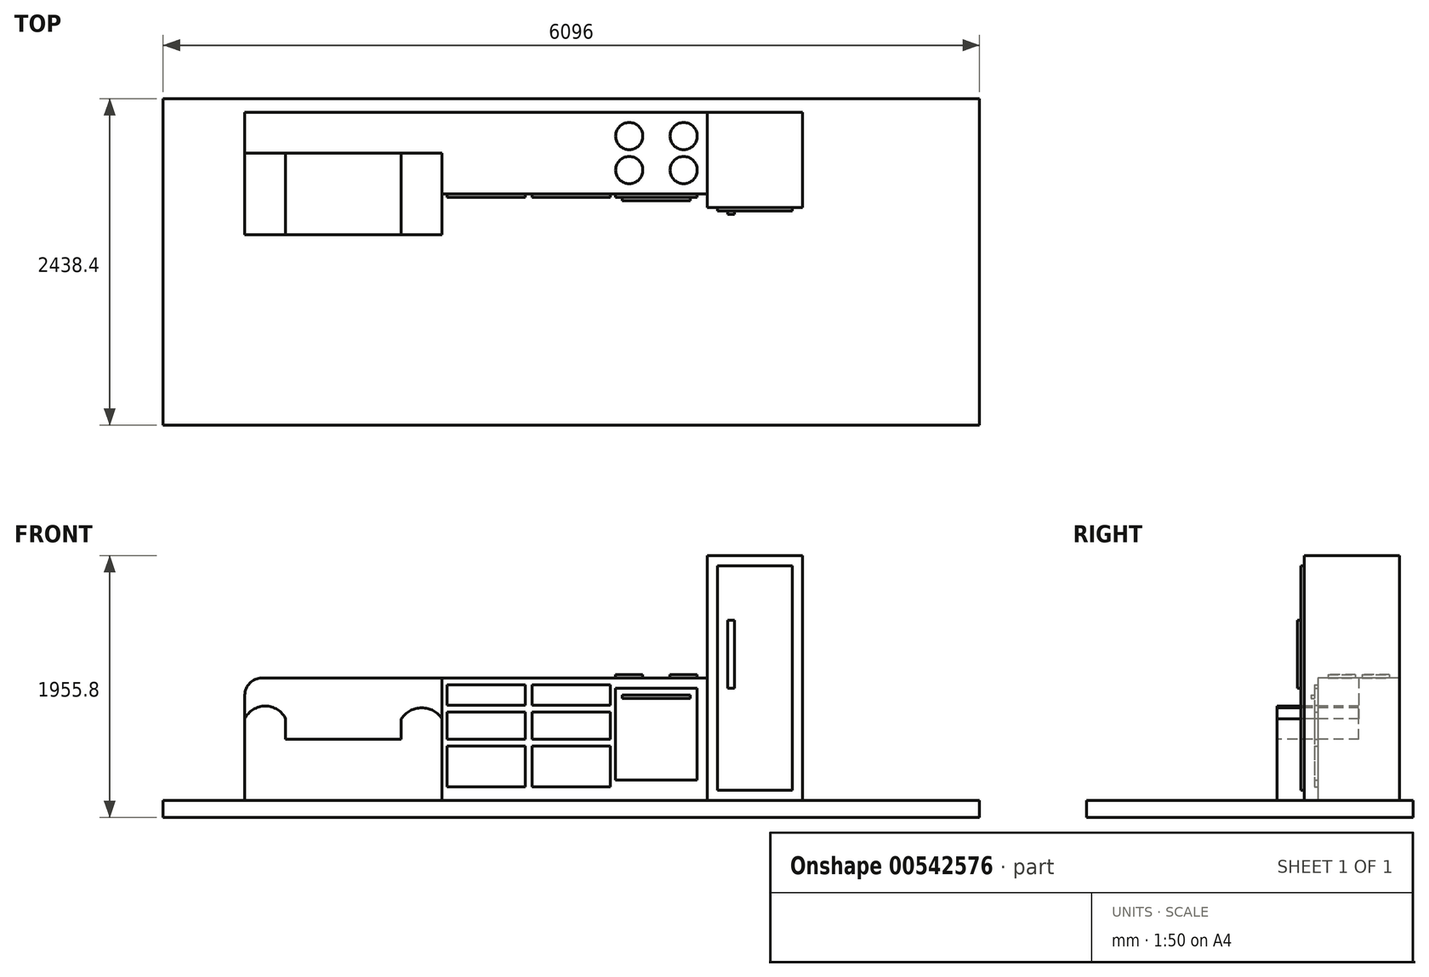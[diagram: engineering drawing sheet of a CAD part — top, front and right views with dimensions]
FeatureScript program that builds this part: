
annotation { "Feature Type Name" : "Feature", "Feature Type Description" : "" }
export const myFeature = defineFeature(function(context is Context, id is Id, definition is map)
    precondition{}
    {
        {
            var Q0;
            Q0=qCreatedBy(makeId("Top.planeOp"),FACE);
            var sketch = newSketch(context, id + "F0", { "sketchPlane" : qUnion([Q0])});
            skLineSegment(sketch, "E0.bottom", {"start": v(-1992.71, 1218.7) * mm, "end": v(4103.29, 1218.7) * mm});
            skLineSegment(sketch, "E0.top", {"start": v(-1992.71, -1219.7) * mm, "end": v(4103.29, -1219.7) * mm});
            skLineSegment(sketch, "E0.left", {"start": v(-1992.71, 1218.7) * mm, "end": v(-1992.71, -1219.7) * mm});
            skLineSegment(sketch, "E0.right", {"start": v(4103.29, 1218.7) * mm, "end": v(4103.29, -1219.7) * mm});
            skSolve(sketch);
        }
        {
            var Q0;
            Q0=makeQuery(id+"F0.imprint","IMPRINT",FACE,{"disambiguationData":[TD([[makeQuery(id+"F0.imprint","IMPRINT",EDGE,{"derivedFrom":sQuery(id+"F0.wireOp",EDGE,"E0.bottom")}),-1.0]])]});
            extrude(context, id + "F1", {"entities" : qUnion([Q0]), "depth" : 127 * mm, "offsetDistance" : 25.4 * mm});
        }
        {
            var Q0;
            Q0=makeQuery(id+"F1.opExtrude","CAP_FACE",FACE,{"disambiguationData":[OSD([sQuery(id+"F0.wireOp",EDGE,"E0.bottom"),sQuery(id+"F0.wireOp",EDGE,"E0.top"),sQuery(id+"F0.wireOp",EDGE,"E0.left"),sQuery(id+"F0.wireOp",EDGE,"E0.right")])],"isStart":false});
            var sketch = newSketch(context, id + "F2", { "sketchPlane" : qUnion([Q0])});
            skLineSegment(sketch, "E1.bottom", {"start": v(-1383.11, 1117.1) * mm, "end": v(2071.29, 1117.1) * mm});
            skLineSegment(sketch, "E1.top", {"start": v(90.09, 507.5) * mm, "end": v(2071.29, 507.5) * mm});
            skLineSegment(sketch, "E1.left", {"start": v(-1383.11, 1117.1) * mm, "end": v(-1383.11, 507.5) * mm});
            skLineSegment(sketch, "E1.right", {"start": v(2071.29, 1117.1) * mm, "end": v(2071.29, 507.5) * mm});
            skLineSegment(sketch, "E2.bottom", {"start": v(2782.49, 1117.1) * mm, "end": v(2071.29, 1117.1) * mm});
            skLineSegment(sketch, "E2.top", {"start": v(2782.49, 405.9) * mm, "end": v(2071.29, 405.9) * mm});
            skLineSegment(sketch, "E2.left", {"start": v(2782.49, 1117.1) * mm, "end": v(2782.49, 405.9) * mm});
            skLineSegment(sketch, "E2.right", {"start": v(2071.29, 1117.1) * mm, "end": v(2071.29, 405.9) * mm});
            skLineSegment(sketch, "E3.top", {"start": v(-1383.11, 202.7) * mm, "end": v(90.09, 202.7) * mm});
            skLineSegment(sketch, "E3.left", {"start": v(-1383.11, 507.5) * mm, "end": v(-1383.11, 202.7) * mm});
            skLineSegment(sketch, "E3.right", {"start": v(90.09, 507.5) * mm, "end": v(90.09, 202.7) * mm});
            skLineSegment(sketch, "E4", {"start": v(90.09, 507.5) * mm, "end": v(90.09, 1117.1) * mm});
            skLineSegment(sketch, "E5", {"start": v(1309.29, 507.5) * mm, "end": v(1309.29, 1117.1) * mm});
            skSolve(sketch);
        }
        {
            var Q0;
            {var subQ0=sQuery(id+"F2.wireOp",EDGE,"E1.left");Q0=makeQuery(id+"F2.imprint","IMPRINT",FACE,{"disambiguationData":[TD([[makeQuery(id+"F2.imprint","IMPRINT",EDGE,{"derivedFrom":subQ0}),1.0]])]});}
            var Q1;
            {var subQ0=sQuery(id+"F2.wireOp",EDGE,"E4");Q1=makeQuery(id+"F2.imprint","IMPRINT",FACE,{"disambiguationData":[TD([[makeQuery(id+"F2.imprint","IMPRINT",EDGE,{"derivedFrom":subQ0}),-1.0]])]});}
            var Q2;
            {var subQ3=sQuery(id+"F2.wireOp",EDGE,"E5");Q2=makeQuery(id+"F2.imprint","IMPRINT",FACE,{"disambiguationData":[TD([[makeQuery(id+"F2.imprint","IMPRINT",EDGE,{"derivedFrom":subQ3}),-1.0]])]});}
            extrude(context, id + "F3", {"entities" : qUnion([Q0, Q1, Q2]), "operationType" : NewBodyOperationType.ADD, "depth" : 914.4 * mm, "offsetDistance" : 25.4 * mm});
        }
        {
            var Q0;
            {var subQ1=sQuery(id+"F2.wireOp",EDGE,"E2.bottom");Q0=makeQuery(id+"F2.imprint","IMPRINT",FACE,{"disambiguationData":[TD([[makeQuery(id+"F2.imprint","IMPRINT",EDGE,{"derivedFrom":subQ1}),1.0]])]});}
            extrude(context, id + "F4", {"entities" : qUnion([Q0]), "operationType" : NewBodyOperationType.ADD, "depth" : 1828.8 * mm, "offsetDistance" : 25.4 * mm});
        }
        {
            var Q0;
            Q0=makeQuery(id+"F3.opExtrude","CAP_FACE",FACE,{"disambiguationData":[OSD([sQuery(id+"F2.wireOp",EDGE,"E1.bottom"),sQuery(id+"F2.wireOp",EDGE,"E1.top"),sQuery(id+"F2.wireOp",EDGE,"E1.left"),sQuery(id+"F2.wireOp",EDGE,"E2.right"),sQuery(id+"F2.wireOp",EDGE,"E3.top"),sQuery(id+"F2.wireOp",EDGE,"E3.left"),sQuery(id+"F2.wireOp",EDGE,"E3.right")])],"isStart":false});
            var sketch = newSketch(context, id + "F5", { "sketchPlane" : qUnion([Q0])});
            skLineSegment(sketch, "E6", {"start": v(1309.29, 1117.1) * mm, "end": v(1309.29, 507.5) * mm});
            skLineSegment(sketch, "E7.bottom", {"start": v(1487.09, 939.3) * mm, "end": v(1893.49, 939.3) * mm, "construction": true});
            skLineSegment(sketch, "E7.top", {"start": v(1487.09, 685.3) * mm, "end": v(1893.49, 685.3) * mm, "construction": true});
            skLineSegment(sketch, "E7.left", {"start": v(1487.09, 939.3) * mm, "end": v(1487.09, 685.3) * mm, "construction": true});
            skLineSegment(sketch, "E7.right", {"start": v(1893.49, 939.3) * mm, "end": v(1893.49, 685.3) * mm, "construction": true});
            skPoint(sketch, "E7.middle", {"position": v(1690.29, 812.3) * mm});
            skCircle(sketch, "E8", {"center": v(1487.09, 939.3) * mm, "radius": 101.6 * mm});
            skCircle(sketch, "E9", {"center": v(1893.49, 939.3) * mm, "radius": 101.6 * mm});
            skCircle(sketch, "E10", {"center": v(1893.49, 685.3) * mm, "radius": 101.6 * mm});
            skCircle(sketch, "E11", {"center": v(1487.09, 685.3) * mm, "radius": 101.6 * mm});
            skSolve(sketch);
        }
        {
            var Q0;
            Q0=makeQuery(id+"F5.imprint","IMPRINT",FACE,{"disambiguationData":[TD([[makeQuery(id+"F5.imprint","IMPRINT",EDGE,{"derivedFrom":sQuery(id+"F5.wireOp",EDGE,"E9")}),1.0]])]});
            var Q1;
            Q1=makeQuery(id+"F5.imprint","IMPRINT",FACE,{"disambiguationData":[TD([[makeQuery(id+"F5.imprint","IMPRINT",EDGE,{"derivedFrom":sQuery(id+"F5.wireOp",EDGE,"E8")}),1.0]])]});
            var Q2;
            Q2=makeQuery(id+"F5.imprint","IMPRINT",FACE,{"disambiguationData":[TD([[makeQuery(id+"F5.imprint","IMPRINT",EDGE,{"derivedFrom":sQuery(id+"F5.wireOp",EDGE,"E11")}),1.0]])]});
            var Q3;
            Q3=makeQuery(id+"F5.imprint","IMPRINT",FACE,{"disambiguationData":[TD([[makeQuery(id+"F5.imprint","IMPRINT",EDGE,{"derivedFrom":sQuery(id+"F5.wireOp",EDGE,"E10")}),1.0]])]});
            extrude(context, id + "F6", {"entities" : qUnion([Q0, Q1, Q2, Q3]), "operationType" : NewBodyOperationType.ADD, "depth" : 25.4 * mm, "offsetDistance" : 25.4 * mm});
        }
        {
            var Q0;
            Q0=makeQuery(id+"F3.opExtrude","SWEPT_FACE",FACE,{"disambiguationData":[OSD([sQuery(id+"F2.wireOp",EDGE,"E1.top")])]});
            var sketch = newSketch(context, id + "F7", { "sketchPlane" : qUnion([Q0])});
            skLineSegment(sketch, "E12", {"start": v(1309.29, 1041.4) * mm, "end": v(1309.29, 127) * mm});
            skLineSegment(sketch, "E13.bottom", {"start": v(1385.49, 965.2) * mm, "end": v(1995.09, 965.2) * mm});
            skLineSegment(sketch, "E13.top", {"start": v(1385.49, 279.4) * mm, "end": v(1995.09, 279.4) * mm});
            skLineSegment(sketch, "E13.left", {"start": v(1385.49, 965.2) * mm, "end": v(1385.49, 279.4) * mm});
            skLineSegment(sketch, "E13.right", {"start": v(1995.09, 965.2) * mm, "end": v(1995.09, 279.4) * mm});
            skPoint(sketch, "E13.middle", {"position": v(1690.29, 622.3) * mm});
            skSolve(sketch);
        }
        {
            var Q0;
            Q0=makeQuery(id+"F7.imprint","IMPRINT",FACE,{"disambiguationData":[TD([[makeQuery(id+"F7.imprint","IMPRINT",EDGE,{"derivedFrom":sQuery(id+"F7.wireOp",EDGE,"E13.bottom")}),-1.0]])]});
            extrude(context, id + "F8", {"entities" : qUnion([Q0]), "operationType" : NewBodyOperationType.ADD, "depth" : 25.4 * mm, "offsetDistance" : 25.4 * mm});
        }
        {
            var Q0;
            Q0=makeQuery(id+"F8.opExtrude","CAP_FACE",FACE,{"disambiguationData":[OSD([sQuery(id+"F7.wireOp",EDGE,"E13.bottom"),sQuery(id+"F7.wireOp",EDGE,"E13.top"),sQuery(id+"F7.wireOp",EDGE,"E13.left"),sQuery(id+"F7.wireOp",EDGE,"E13.right")])],"isStart":false});
            var sketch = newSketch(context, id + "F9", { "sketchPlane" : qUnion([Q0])});
            skLineSegment(sketch, "E14.bottom", {"start": v(1436.29, 914.4) * mm, "end": v(1944.29, 914.4) * mm});
            skLineSegment(sketch, "E14.top", {"start": v(1436.29, 889) * mm, "end": v(1944.29, 889) * mm});
            skLineSegment(sketch, "E14.left", {"start": v(1436.29, 914.4) * mm, "end": v(1436.29, 889) * mm});
            skLineSegment(sketch, "E14.right", {"start": v(1944.29, 914.4) * mm, "end": v(1944.29, 889) * mm});
            skPoint(sketch, "E14.middle", {"position": v(1690.29, 901.7) * mm});
            skSolve(sketch);
        }
        {
            var Q0;
            Q0=makeQuery(id+"F9.imprint","IMPRINT",FACE,{"disambiguationData":[TD([[makeQuery(id+"F9.imprint","IMPRINT",EDGE,{"derivedFrom":sQuery(id+"F9.wireOp",EDGE,"E14.bottom")}),-1.0]])]});
            extrude(context, id + "F10", {"entities" : qUnion([Q0]), "operationType" : NewBodyOperationType.ADD, "depth" : 25.4 * mm, "offsetDistance" : 25.4 * mm});
        }
        {
            var Q0;
            Q0=makeQuery(id+"F4.opExtrude","SWEPT_FACE",FACE,{"disambiguationData":[OSD([sQuery(id+"F2.wireOp",EDGE,"E2.top")])]});
            var sketch = newSketch(context, id + "F11", { "sketchPlane" : qUnion([Q0])});
            skLineSegment(sketch, "E15.0", {"start": v(2147.49, 203.2) * mm, "end": v(2706.29, 203.2) * mm});
            skLineSegment(sketch, "E15.1", {"start": v(2147.49, 1879.6) * mm, "end": v(2147.49, 203.2) * mm});
            skLineSegment(sketch, "E15.2", {"start": v(2706.29, 1879.6) * mm, "end": v(2147.49, 1879.6) * mm});
            skLineSegment(sketch, "E15.3", {"start": v(2706.29, 203.2) * mm, "end": v(2706.29, 1879.6) * mm});
            skSolve(sketch);
        }
        {
            var Q0;
            Q0=makeQuery(id+"F11.imprint","IMPRINT",FACE,{"disambiguationData":[TD([[makeQuery(id+"F11.imprint","IMPRINT",EDGE,{"derivedFrom":sQuery(id+"F11.wireOp",EDGE,"E15.0")}),1.0]])]});
            extrude(context, id + "F12", {"entities" : qUnion([Q0]), "operationType" : NewBodyOperationType.ADD, "depth" : 25.4 * mm, "offsetDistance" : 25.4 * mm});
        }
        {
            var Q0;
            Q0=makeQuery(id+"F12.opExtrude","CAP_FACE",FACE,{"disambiguationData":[OSD([sQuery(id+"F11.wireOp",EDGE,"E15.0"),sQuery(id+"F11.wireOp",EDGE,"E15.1"),sQuery(id+"F11.wireOp",EDGE,"E15.2"),sQuery(id+"F11.wireOp",EDGE,"E15.3")])],"isStart":false});
            var sketch = newSketch(context, id + "F13", { "sketchPlane" : qUnion([Q0])});
            skLineSegment(sketch, "E16.bottom", {"start": v(2223.69, 1473.2) * mm, "end": v(2274.49, 1473.2) * mm});
            skLineSegment(sketch, "E16.top", {"start": v(2223.69, 965.2) * mm, "end": v(2274.49, 965.2) * mm});
            skLineSegment(sketch, "E16.left", {"start": v(2223.69, 1473.2) * mm, "end": v(2223.69, 965.2) * mm});
            skLineSegment(sketch, "E16.right", {"start": v(2274.49, 1473.2) * mm, "end": v(2274.49, 965.2) * mm});
            skPoint(sketch, "E16.middle", {"position": v(2249.09, 1219.2) * mm});
            skSolve(sketch);
        }
        {
            var Q0;
            Q0=makeQuery(id+"F13.imprint","IMPRINT",FACE,{"disambiguationData":[TD([[makeQuery(id+"F13.imprint","IMPRINT",EDGE,{"derivedFrom":sQuery(id+"F13.wireOp",EDGE,"E16.bottom")}),-1.0]])]});
            extrude(context, id + "F14", {"entities" : qUnion([Q0]), "operationType" : NewBodyOperationType.ADD, "depth" : 25.4 * mm, "offsetDistance" : 25.4 * mm});
        }
        {
            var Q0;
            Q0=makeQuery(id+"F3.opExtrude","SWEPT_FACE",FACE,{"disambiguationData":[OSD([sQuery(id+"F2.wireOp",EDGE,"E1.top")])]});
            var sketch = newSketch(context, id + "F15", { "sketchPlane" : qUnion([Q0])});
            skLineSegment(sketch, "E17.bottom", {"start": v(128.19, 990.6) * mm, "end": v(712.39, 990.6) * mm});
            skLineSegment(sketch, "E17.top", {"start": v(128.19, 838.2) * mm, "end": v(712.39, 838.2) * mm});
            skLineSegment(sketch, "E17.left", {"start": v(128.19, 990.6) * mm, "end": v(128.19, 838.2) * mm});
            skLineSegment(sketch, "E17.right", {"start": v(712.39, 990.6) * mm, "end": v(712.39, 838.2) * mm});
            skPoint(sketch, "E17.middle", {"position": v(420.29, 914.4) * mm});
            skLineSegment(sketch, "E18.bottom", {"start": v(763.19, 990.6) * mm, "end": v(1347.39, 990.6) * mm});
            skLineSegment(sketch, "E18.top", {"start": v(763.19, 838.2) * mm, "end": v(1347.39, 838.2) * mm});
            skLineSegment(sketch, "E18.left", {"start": v(763.19, 990.6) * mm, "end": v(763.19, 838.2) * mm});
            skLineSegment(sketch, "E18.right", {"start": v(1347.39, 990.6) * mm, "end": v(1347.39, 838.2) * mm});
            skPoint(sketch, "E18.middle", {"position": v(1055.29, 914.4) * mm});
            skLineSegment(sketch, "E19.bottom", {"start": v(763.19, 787.4) * mm, "end": v(1347.39, 787.4) * mm});
            skLineSegment(sketch, "E19.top", {"start": v(763.19, 584.2) * mm, "end": v(1347.39, 584.2) * mm});
            skLineSegment(sketch, "E19.left", {"start": v(763.19, 787.4) * mm, "end": v(763.19, 584.2) * mm});
            skLineSegment(sketch, "E19.right", {"start": v(1347.39, 787.4) * mm, "end": v(1347.39, 584.2) * mm});
            skPoint(sketch, "E19.middle", {"position": v(1055.29, 685.8) * mm});
            skLineSegment(sketch, "E20.bottom", {"start": v(128.19, 787.4) * mm, "end": v(712.39, 787.4) * mm});
            skLineSegment(sketch, "E20.top", {"start": v(128.19, 584.2) * mm, "end": v(712.39, 584.2) * mm});
            skLineSegment(sketch, "E20.left", {"start": v(128.19, 787.4) * mm, "end": v(128.19, 584.2) * mm});
            skLineSegment(sketch, "E20.right", {"start": v(712.39, 787.4) * mm, "end": v(712.39, 584.2) * mm});
            skPoint(sketch, "E20.middle", {"position": v(420.29, 685.8) * mm});
            skLineSegment(sketch, "E21.bottom", {"start": v(128.19, 533.4) * mm, "end": v(712.39, 533.4) * mm});
            skLineSegment(sketch, "E21.top", {"start": v(128.19, 228.6) * mm, "end": v(712.39, 228.6) * mm});
            skLineSegment(sketch, "E21.left", {"start": v(128.19, 533.4) * mm, "end": v(128.19, 228.6) * mm});
            skLineSegment(sketch, "E21.right", {"start": v(712.39, 533.4) * mm, "end": v(712.39, 228.6) * mm});
            skLineSegment(sketch, "E22.bottom", {"start": v(763.19, 533.4) * mm, "end": v(1347.39, 533.4) * mm});
            skLineSegment(sketch, "E22.top", {"start": v(763.19, 228.6) * mm, "end": v(1347.39, 228.6) * mm});
            skLineSegment(sketch, "E22.left", {"start": v(763.19, 533.4) * mm, "end": v(763.19, 228.6) * mm});
            skLineSegment(sketch, "E22.right", {"start": v(1347.39, 533.4) * mm, "end": v(1347.39, 228.6) * mm});
            skSolve(sketch);
        }
        {
            var Q0;
            Q0=makeQuery(id+"F15.imprint","IMPRINT",FACE,{"disambiguationData":[TD([[makeQuery(id+"F15.imprint","IMPRINT",EDGE,{"derivedFrom":sQuery(id+"F15.wireOp",EDGE,"E17.bottom")}),-1.0]])]});
            var Q1;
            Q1=makeQuery(id+"F15.imprint","IMPRINT",FACE,{"disambiguationData":[TD([[makeQuery(id+"F15.imprint","IMPRINT",EDGE,{"derivedFrom":sQuery(id+"F15.wireOp",EDGE,"E18.bottom")}),-1.0]])]});
            var Q2;
            Q2=makeQuery(id+"F15.imprint","IMPRINT",FACE,{"disambiguationData":[TD([[makeQuery(id+"F15.imprint","IMPRINT",EDGE,{"derivedFrom":sQuery(id+"F15.wireOp",EDGE,"E20.bottom")}),-1.0]])]});
            var Q3;
            Q3=makeQuery(id+"F15.imprint","IMPRINT",FACE,{"disambiguationData":[TD([[makeQuery(id+"F15.imprint","IMPRINT",EDGE,{"derivedFrom":sQuery(id+"F15.wireOp",EDGE,"E19.bottom")}),-1.0]])]});
            var Q4;
            Q4=makeQuery(id+"F15.imprint","IMPRINT",FACE,{"disambiguationData":[TD([[makeQuery(id+"F15.imprint","IMPRINT",EDGE,{"derivedFrom":sQuery(id+"F15.wireOp",EDGE,"E21.bottom")}),-1.0]])]});
            var Q5;
            Q5=makeQuery(id+"F15.imprint","IMPRINT",FACE,{"disambiguationData":[TD([[makeQuery(id+"F15.imprint","IMPRINT",EDGE,{"derivedFrom":sQuery(id+"F15.wireOp",EDGE,"E22.bottom")}),-1.0]])]});
            extrude(context, id + "F16", {"entities" : qUnion([Q0, Q1, Q2, Q3, Q4, Q5]), "operationType" : NewBodyOperationType.ADD, "depth" : 25.4 * mm, "offsetDistance" : 25.4 * mm});
        }
        {
            var Q0;
            Q0=makeQuery(id+"F3.opExtrude","SWEPT_FACE",FACE,{"disambiguationData":[OSD([sQuery(id+"F2.wireOp",EDGE,"E3.top")])]});
            var sketch = newSketch(context, id + "F17", { "sketchPlane" : qUnion([Q0])});
            skLineSegment(sketch, "E23.bottom", {"start": v(-1383.11, 127) * mm, "end": v(-1078.31, 127) * mm});
            skLineSegment(sketch, "E23.top", {"start": v(-1383.11, 736.6) * mm, "end": v(-1078.31, 736.6) * mm});
            skLineSegment(sketch, "E23.left", {"start": v(-1383.11, 127) * mm, "end": v(-1383.11, 736.6) * mm});
            skLineSegment(sketch, "E23.right", {"start": v(-1078.31, 127) * mm, "end": v(-1078.31, 736.6) * mm});
            skLineSegment(sketch, "E24.bottom", {"start": v(90.09, 127) * mm, "end": v(-214.71, 127) * mm});
            skLineSegment(sketch, "E24.top", {"start": v(90.09, 736.6) * mm, "end": v(-214.71, 736.6) * mm});
            skLineSegment(sketch, "E24.left", {"start": v(90.09, 127) * mm, "end": v(90.09, 736.6) * mm});
            skLineSegment(sketch, "E24.right", {"start": v(-214.71, 127) * mm, "end": v(-214.71, 736.6) * mm});
            skArc(sketch, "E25", {"start": v(-1078.31, 736.6) * mm, "mid": v(-1230.71, 832.41) * mm, "end": v(-1383.11, 736.6) * mm});
            skPoint(sketch, "E25.centerSnap0", {"position": v(-1230.71, 736.6) * mm});
            skArc(sketch, "E26", {"start": v(90.09, 736.6) * mm, "mid": v(-62.31, 818.72) * mm, "end": v(-214.71, 736.6) * mm});
            skPoint(sketch, "E26.centerSnap0", {"position": v(-62.31, 736.6) * mm});
            skLineSegment(sketch, "E27", {"start": v(-1078.31, 584.2) * mm, "end": v(-214.71, 584.2) * mm});
            skSolve(sketch);
        }
        {
            var Q0;
            {var subQ1=sQuery(id+"F17.wireOp",EDGE,"E25");Q0=makeQuery(id+"F17.imprint","IMPRINT",FACE,{"disambiguationData":[TD([[makeQuery(id+"F17.imprint","IMPRINT",EDGE,{"derivedFrom":subQ1}),-1.0]])]});}
            extrude(context, id + "F18", {"entities" : qUnion([Q0]), "operationType" : NewBodyOperationType.REMOVE, "oppositeDirection" : true, "depth" : 609.6 * mm, "offsetDistance" : 25.4 * mm});
        }
        {
            var Q0;
            Q0=makeQuery(id+"F18.boolean.opBoolean","COPY",EDGE,{"derivedFrom":makeQuery(id+"F18.opExtrude","CAP_EDGE",EDGE,{"disambiguationData":[OSD([sQuery(id+"F2.wireOp",EDGE,"E3.top")])],"isStart":false})});
            var Q1;
            Q1=makeQuery(id+"F3.opExtrude","CAP_EDGE",EDGE,{"disambiguationData":[OSD([sQuery(id+"F2.wireOp",EDGE,"E1.left"),sQuery(id+"F2.wireOp",EDGE,"E3.left")])],"isStart":false});
            fillet(context, id + "F19", {"entities" : qUnion([Q0, Q1]), "radius" : 127 * mm, "tangentPropagation" : true, "allowEdgeOverflow" : false});
        }
    });
